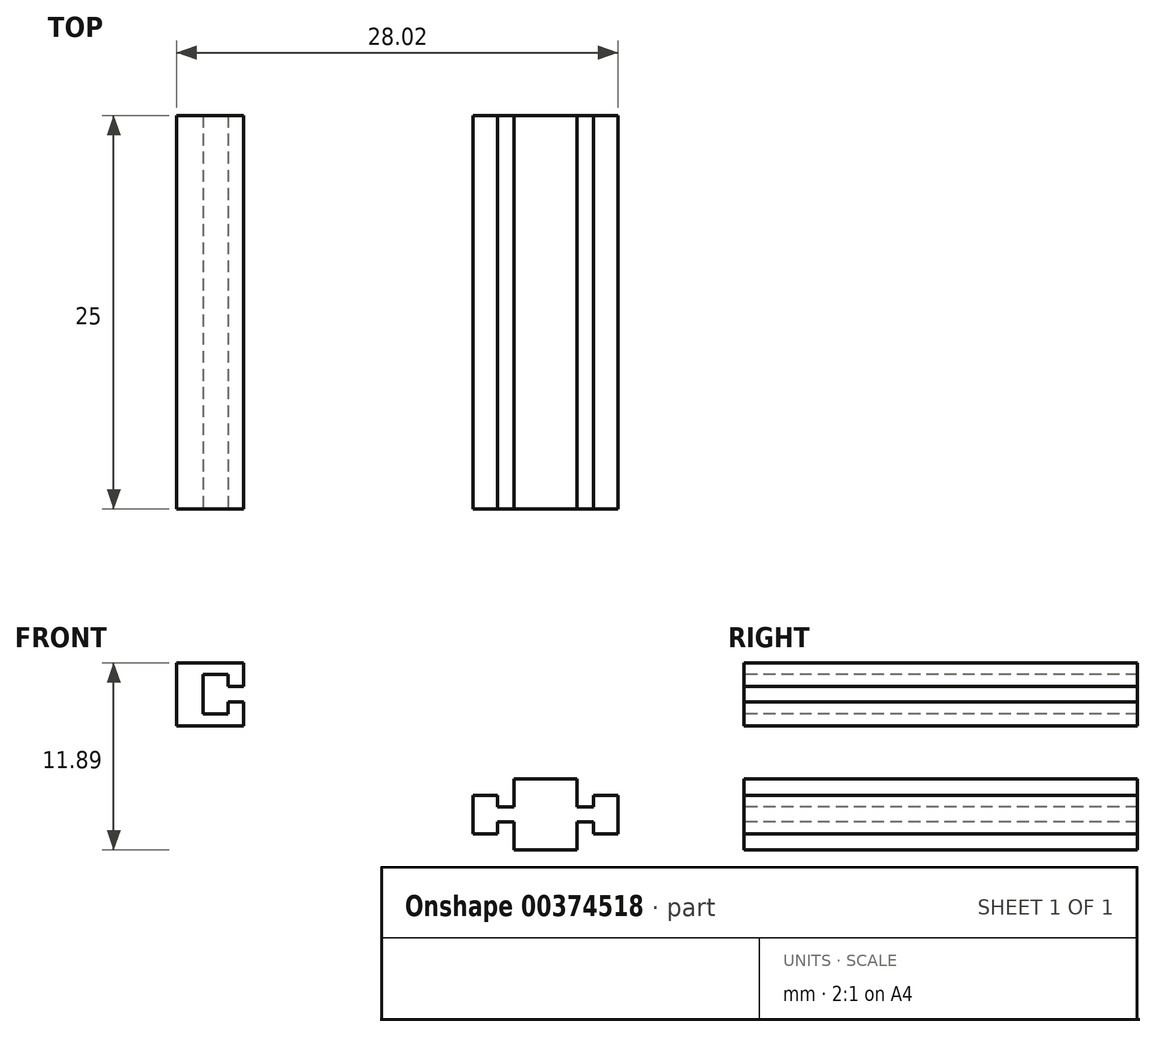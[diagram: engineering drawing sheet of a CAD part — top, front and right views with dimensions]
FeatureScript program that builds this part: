
annotation { "Feature Type Name" : "Feature", "Feature Type Description" : "" }
export const myFeature = defineFeature(function(context is Context, id is Id, definition is map)
    precondition{}
    {
        {
            var Q0;
            Q0=qCreatedBy(makeId("Front.planeOp"),FACE);
            var sketch = newSketch(context, id + "F0", { "sketchPlane" : qUnion([Q0])});
            skLineSegment(sketch, "E0.bottom", {"start": v(-22.28, 16.52) * mm, "end": v(-26.28, 16.52) * mm});
            skLineSegment(sketch, "E0.top", {"start": v(-22.28, 21.02) * mm, "end": v(-26.28, 21.02) * mm});
            skLineSegment(sketch, "E0.left", {"start": v(-22.28, 16.52) * mm, "end": v(-22.28, 21.02) * mm});
            skLineSegment(sketch, "E0.right", {"start": v(-26.28, 16.52) * mm, "end": v(-26.28, 21.02) * mm});
            skPoint(sketch, "E0.middle", {"position": v(-24.28, 18.77) * mm});
            skLineSegment(sketch, "E1.bottom", {"start": v(-22.28, 18.3) * mm, "end": v(-21.23, 18.3) * mm});
            skLineSegment(sketch, "E1.top", {"start": v(-22.28, 19.24) * mm, "end": v(-21.23, 19.24) * mm});
            skLineSegment(sketch, "E1.left", {"start": v(-22.28, 18.3) * mm, "end": v(-22.28, 19.24) * mm});
            skLineSegment(sketch, "E1.right", {"start": v(-21.23, 18.3) * mm, "end": v(-21.23, 19.24) * mm});
            skPoint(sketch, "E1.middle", {"position": v(-21.76, 18.77) * mm});
            skPoint(sketch, "E1.middle.positionSnap0", {"position": v(-22.28, 18.77) * mm});
            skPoint(sketch, "E1.centerSnap0", {"position": v(-22.28, 18.77) * mm});
            skLineSegment(sketch, "E2.bottom", {"start": v(-21.23, 17.54) * mm, "end": v(-19.68, 17.54) * mm});
            skLineSegment(sketch, "E2.top", {"start": v(-21.23, 20) * mm, "end": v(-19.68, 20) * mm});
            skLineSegment(sketch, "E2.left", {"start": v(-21.23, 17.54) * mm, "end": v(-21.23, 20) * mm});
            skLineSegment(sketch, "E2.right", {"start": v(-19.68, 17.54) * mm, "end": v(-19.68, 20) * mm});
            skPoint(sketch, "E2.middle", {"position": v(-20.46, 18.77) * mm});
            skLineSegment(sketch, "E3.bottom", {"start": v(-26.28, 18.3) * mm, "end": v(-27.33, 18.3) * mm});
            skLineSegment(sketch, "E3.top", {"start": v(-26.28, 19.24) * mm, "end": v(-27.33, 19.24) * mm});
            skLineSegment(sketch, "E3.left", {"start": v(-26.28, 18.3) * mm, "end": v(-26.28, 19.24) * mm});
            skLineSegment(sketch, "E3.right", {"start": v(-27.33, 18.3) * mm, "end": v(-27.33, 19.24) * mm});
            skPoint(sketch, "E3.middle", {"position": v(-26.8, 18.77) * mm});
            skLineSegment(sketch, "E4.bottom", {"start": v(-27.33, 17.54) * mm, "end": v(-28.88, 17.54) * mm});
            skLineSegment(sketch, "E4.top", {"start": v(-27.33, 20) * mm, "end": v(-28.88, 20) * mm});
            skLineSegment(sketch, "E4.left", {"start": v(-27.33, 17.54) * mm, "end": v(-27.33, 20) * mm});
            skLineSegment(sketch, "E4.right", {"start": v(-28.88, 17.54) * mm, "end": v(-28.88, 20) * mm});
            skPoint(sketch, "E4.middle", {"position": v(-28.1, 18.77) * mm});
            skPoint(sketch, "E4.cornerSnap0", {"position": v(-27.33, 18.77) * mm});
            skSolve(sketch);
        }
        {
            var Q0;
            {var subQ3=sQuery(id+"F0.wireOp",EDGE,"E4.bottom");Q0=makeQuery(id+"F0.imprint","IMPRINT",FACE,{"disambiguationData":[TD([[makeQuery(id+"F0.imprint","IMPRINT",EDGE,{"derivedFrom":subQ3}),-1.0]])]});}
            var Q1;
            {var subQ0=sQuery(id+"F0.wireOp",EDGE,"E3.bottom");Q1=makeQuery(id+"F0.imprint","IMPRINT",FACE,{"disambiguationData":[TD([[makeQuery(id+"F0.imprint","IMPRINT",EDGE,{"derivedFrom":subQ0}),-1.0]])]});}
            var Q2;
            {var subQ3=sQuery(id+"F0.wireOp",EDGE,"E0.bottom");Q2=makeQuery(id+"F0.imprint","IMPRINT",FACE,{"disambiguationData":[TD([[makeQuery(id+"F0.imprint","IMPRINT",EDGE,{"derivedFrom":subQ3}),-1.0]])]});}
            var Q3;
            {var subQ0=sQuery(id+"F0.wireOp",EDGE,"E1.bottom");Q3=makeQuery(id+"F0.imprint","IMPRINT",FACE,{"disambiguationData":[TD([[makeQuery(id+"F0.imprint","IMPRINT",EDGE,{"derivedFrom":subQ0}),1.0]])]});}
            var Q4;
            {var subQ3=sQuery(id+"F0.wireOp",EDGE,"E2.bottom");Q4=makeQuery(id+"F0.imprint","IMPRINT",FACE,{"disambiguationData":[TD([[makeQuery(id+"F0.imprint","IMPRINT",EDGE,{"derivedFrom":subQ3}),1.0]])]});}
            extrude(context, id + "F1", {"entities" : qUnion([Q0, Q1, Q2, Q3, Q4]), "oppositeDirection" : true, "depth" : 25 * mm});
        }
        {
            var Q0;
            Q0=qCreatedBy(makeId("Front.planeOp"),FACE);
            var sketch = newSketch(context, id + "F2", { "sketchPlane" : qUnion([Q0])});
            skLineSegment(sketch, "E5.bottom", {"start": v(-47.7, 24.4) * mm, "end": v(-46.04, 24.4) * mm});
            skLineSegment(sketch, "E5.top", {"start": v(-47.7, 28.4) * mm, "end": v(-46.04, 28.4) * mm});
            skLineSegment(sketch, "E5.left", {"start": v(-47.7, 24.4) * mm, "end": v(-47.7, 28.4) * mm});
            skLineSegment(sketch, "E5.right", {"start": v(-46.04, 24.4) * mm, "end": v(-46.04, 28.4) * mm});
            skLineSegment(sketch, "E6.bottom", {"start": v(-46.04, 28.4) * mm, "end": v(-43.44, 28.4) * mm});
            skLineSegment(sketch, "E6.top", {"start": v(-46.04, 27.66) * mm, "end": v(-43.44, 27.66) * mm});
            skLineSegment(sketch, "E6.left", {"start": v(-46.04, 28.4) * mm, "end": v(-46.04, 27.66) * mm});
            skLineSegment(sketch, "E6.right", {"start": v(-43.44, 28.4) * mm, "end": v(-43.44, 27.66) * mm});
            skLineSegment(sketch, "E7.bottom", {"start": v(-46.04, 24.4) * mm, "end": v(-43.44, 24.4) * mm});
            skLineSegment(sketch, "E7.top", {"start": v(-46.04, 25.16) * mm, "end": v(-43.44, 25.16) * mm});
            skLineSegment(sketch, "E7.left", {"start": v(-46.04, 24.4) * mm, "end": v(-46.04, 25.16) * mm});
            skLineSegment(sketch, "E7.right", {"start": v(-43.44, 24.4) * mm, "end": v(-43.44, 25.16) * mm});
            skLineSegment(sketch, "E8.bottom", {"start": v(-43.44, 25.16) * mm, "end": v(-44.44, 25.16) * mm});
            skLineSegment(sketch, "E8.top", {"start": v(-43.44, 25.9) * mm, "end": v(-44.44, 25.9) * mm});
            skLineSegment(sketch, "E8.left", {"start": v(-43.44, 25.16) * mm, "end": v(-43.44, 25.9) * mm});
            skLineSegment(sketch, "E8.right", {"start": v(-44.44, 25.16) * mm, "end": v(-44.44, 25.9) * mm});
            skLineSegment(sketch, "E9.bottom", {"start": v(-43.44, 26.9) * mm, "end": v(-44.44, 26.9) * mm});
            skLineSegment(sketch, "E9.top", {"start": v(-43.44, 27.66) * mm, "end": v(-44.44, 27.66) * mm});
            skLineSegment(sketch, "E9.left", {"start": v(-43.44, 26.9) * mm, "end": v(-43.44, 27.66) * mm});
            skLineSegment(sketch, "E9.right", {"start": v(-44.44, 26.9) * mm, "end": v(-44.44, 27.66) * mm});
            skSolve(sketch);
        }
        {
            var Q0;
            Q0 = qSketchRegion(id + "F2", true);
            extrude(context, id + "F3", {"entities" : qUnion([Q0]), "oppositeDirection" : true, "depth" : 25 * mm});
        }
    });
